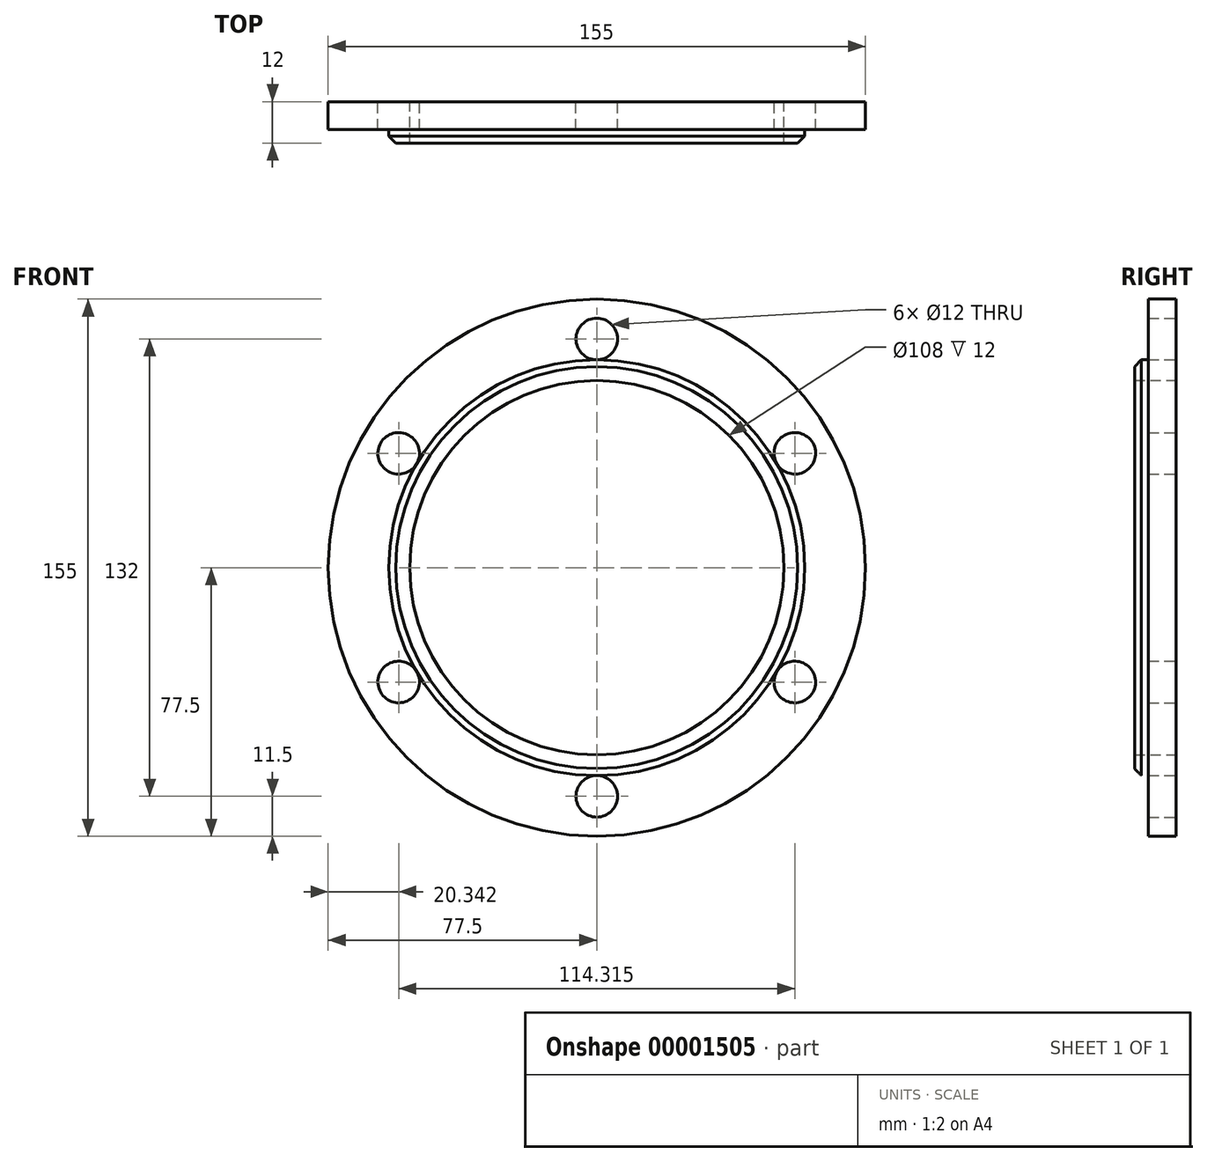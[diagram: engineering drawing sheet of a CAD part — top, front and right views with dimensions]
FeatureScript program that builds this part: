
annotation { "Feature Type Name" : "Feature", "Feature Type Description" : "" }
export const myFeature = defineFeature(function(context is Context, id is Id, definition is map)
    precondition{}
    {
        {
            var Q0;
            Q0=qCreatedBy(makeId("Front.planeOp"),FACE);
            var sketch = newSketch(context, id + "F0", { "sketchPlane" : qUnion([Q0])});
            skCircle(sketch, "E0", {"center": v(0, 0) * mm, "radius": 77.5 * mm});
            skCircle(sketch, "E1", {"center": v(0, 0) * mm, "radius": 54 * mm});
            skCircle(sketch, "E2", {"center": v(0, 66) * mm, "radius": 6 * mm});
            skCircle(sketch, "E3", {"center": v(0, 0) * mm, "radius": 66 * mm, "construction": true});
            skSolve(sketch);
        }
        {
            var Q0;
            Q0 = qSketchRegion(id + "F0", true);
            var Q1;
            Q1=makeQuery(id+"F0.imprint","IMPRINT",FACE,{"disambiguationData":[TD([[makeQuery(id+"F0.imprint","IMPRINT",EDGE,{"derivedFrom":sQuery(id+"F0.wireOp",EDGE,"E2")}),1.0]])]});
            extrude(context, id + "F1", {"entities" : qUnion([Q0, Q1]), "depth" : 8 * mm});
        }
        {
            var Q0;
            Q0=makeQuery(id+"F1.opExtrude","CAP_FACE",FACE,{"disambiguationData":[OSD([sQuery(id+"F0.wireOp",EDGE,"E0"),sQuery(id+"F0.wireOp",EDGE,"E1")])],"isStart":false});
            var sketch = newSketch(context, id + "F2", { "sketchPlane" : qUnion([Q0])});
            skCircle(sketch, "E4", {"center": v(0, 0) * mm, "radius": 60 * mm});
            skCircle(sketch, "E5.0", {"center": v(0, 0) * mm, "radius": 54 * mm});
            skSolve(sketch);
        }
        {
            var Q0;
            Q0 = qSketchRegion(id + "F2", true);
            extrude(context, id + "F3", {"entities" : qUnion([Q0]), "operationType" : NewBodyOperationType.ADD, "depth" : 4 * mm});
        }
        {
            var Q0;
            Q0=makeQuery(id+"F3.opExtrude","CAP_EDGE",EDGE,{"disambiguationData":[OSD([sQuery(id+"F2.wireOp",EDGE,"E4")])],"isStart":false});
            chamfer(context, id + "F4", {"entities" : qUnion([Q0]), "width" : 2 * mm, "tangentPropagation" : true});
        }
        {
            var Q0;
            Q0=makeQuery(id+"F0.imprint","IMPRINT",FACE,{"disambiguationData":[TD([[makeQuery(id+"F0.imprint","IMPRINT",EDGE,{"derivedFrom":sQuery(id+"F0.wireOp",EDGE,"E2")}),1.0]])]});
            var Q1;
            Q1=sQuery(id+"F0.wireOp",EDGE,"E2");
            extrude(context, id + "F5", {"entities" : qUnion([Q0]), "operationType" : NewBodyOperationType.REMOVE, "surfaceEntities" : qUnion([Q1]), "endBound" : BoundingType.UP_TO_NEXT, "depth" : 25 * mm});
        }
        {
            var Q0;
            Q0=makeQuery(id+"F5.boolean.opBoolean","COPY",FACE,{"derivedFrom":makeQuery(id+"F5.opExtrude","SWEPT_FACE",FACE,{"disambiguationData":[OSD([sQuery(id+"F0.wireOp",EDGE,"E2")])]})});
            var Q1;
            Q1=makeQuery(id+"F1.opExtrude","SWEPT_BODY",BODY,{"disambiguationData":[OSD([sQuery(id+"F0.wireOp",EDGE,"E0"),sQuery(id+"F0.wireOp",EDGE,"E1")])]});
            var Q2;
            Q2=sQuery(id+"F0.wireOp",EDGE,"E1");
            circularPattern(context, id + "F6", {"faces" : qUnion([Q0]), "axis" : qUnion([Q2]), "angle" : 360 * degree, "instanceCount" : 6, "equalSpace" : true, "patternType" : PatternType.FACE});
        }
    });
